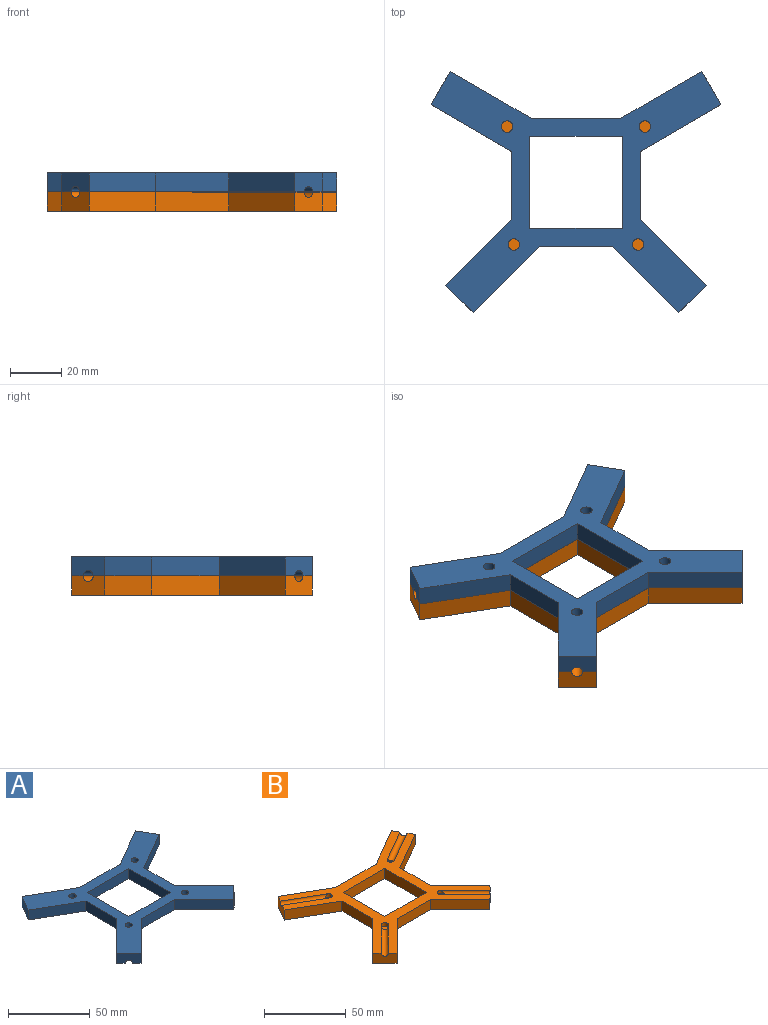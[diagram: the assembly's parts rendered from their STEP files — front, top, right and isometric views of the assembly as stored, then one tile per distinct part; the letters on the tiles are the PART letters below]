
ASSEMBLY  parts=2 mates=1
PART A: 33 faces, bbox 113.2x94.1x7.5 mm
  f0: plane 35x7.5mm, normal (0,1,0), area 260.5mm2, adj f8,f16,f17,f29,f30,f31
  f1: plane 28.79x7.5mm, normal (0,-1,0), area 214.3mm2, adj f2,f16,f23,f29,f31,f32
  f2: plane 25.81x25.81mm, normal (-0.71,-0.71,0), area 273.7mm2, adj f1,f3,f16,f29
  f3: plane 10.61x10.61mm, normal (0.71,-0.71,0), area 104.5mm2, adj f2,f4,f11,f16,f29
  f4: plane 25.81x25.81mm, normal (0.71,0.71,0), area 273.7mm2, adj f3,f5,f16,f29
  f5: plane 26.4x7.5mm, normal (1,0,0), area 198mm2, adj f4,f6,f16,f29
  f6: plane 31.61x18.25mm, normal (0.5,-0.87,0), area 273.7mm2, adj f5,f7,f16,f29
  f7: plane 12.99x7.5mm, normal (0.87,0.5,0), area 104.5mm2, adj f6,f8,f10,f16,f29
  f8: plane 31.61x18.25mm, normal (-0.5,0.87,0), area 273.7mm2, adj f0,f7,f16,f29
  f9: cylinder r=2.25mm len=7.5mm, axis (0,0,1), area 95.9mm2, adj f10,f16,f29
  f10: cylinder r=2.25mm len=28.23mm, axis (0.87,0.5,0), area 201.9mm2, adj f7,f9,f29
  f11: cylinder r=2.25mm len=24.4mm, axis (0.71,-0.71,0), area 201.9mm2, adj f3,f12,f29
  f12: cylinder r=2.25mm len=7.5mm, axis (0,0,1), area 95.9mm2, adj f11,f16,f29
  f13: plane 36x7.5mm, normal (-1,0,0), area 270mm2, adj f14,f15,f16,f29
  f14: plane 36x7.5mm, normal (0,-1,0), area 267.9mm2, adj f13,f16,f28,f29,f30,f31
  f15: plane 36x7.5mm, normal (0,1,0), area 267.9mm2, adj f13,f16,f28,f29,f31,f32
  f16: plane 113.21x94.05mm, normal (0,0,1), area 3120.2mm2, adj f0,f1,f2,f3,f4,f5,f6,f7
  f17: plane 31.61x18.25mm, normal (0.5,0.87,0), area 269.5mm2, adj f0,f16,f18,f31
  f18: plane 12.99x7.5mm, normal (-0.87,0.5,0), area 103.3mm2, adj f16,f17,f19,f24,f31
  f19: plane 31.61x18.25mm, normal (-0.5,-0.87,0), area 269.5mm2, adj f16,f18,f20,f31
  f20: plane 26.4x7.39mm, normal (-1,0,0), area 195mm2, adj f16,f19,f21,f31
  f21: plane 25.81x25.81mm, normal (-0.71,0.71,0), area 269.5mm2, adj f16,f20,f22,f31
  f22: plane 10.61x10.61mm, normal (-0.71,-0.71,0), area 103.3mm2, adj f16,f21,f23,f25,f31
  f23: plane 25.81x25.81mm, normal (0.71,-0.71,0), area 269.5mm2, adj f1,f16,f22,f31
  f24: cylinder r=2.25mm len=28.13mm, axis (-0.87,0.5,0), area 195.1mm2, adj f18,f27,f31
  f25: cylinder r=2.25mm len=24.31mm, axis (-0.71,-0.71,0), area 195.1mm2, adj f22,f26,f31
  f26: cylinder r=2.25mm len=7.39mm, axis (0,0,1), area 95.1mm2, adj f16,f25,f31
  f27: cylinder r=2.25mm len=7.39mm, axis (0,0,1), area 95.1mm2, adj f16,f24,f31
  f28: plane 36x7.39mm, normal (1,0,0), area 265.9mm2, adj f14,f15,f16,f31
  f29: plane 94.05x56.61mm, normal (0,0,-1), area 1306mm2, adj f0,f1,f2,f3,f4,f5,f6,f7
  f30: plane 7x0.11mm, normal (-1,0,0), area 0.8mm2, adj f0,f14,f29,f31
  f31: plane 94.05x56.61mm, normal (0,0,-1), area 1306.3mm2, adj f0,f1,f14,f15,f17,f18,f19,f20
  f32: plane 7x0.11mm, normal (-1,0,0), area 0.8mm2, adj f1,f15,f29,f31
PART B: 34 faces, bbox 113.2x94.1x7.5 mm
  f0: plane 113.21x94.05mm, normal (0,0,-1), area 3183.8mm2, adj f1,f2,f3,f4,f5,f6,f7,f8
  f1: plane 35x7.5mm, normal (0,1,0), area 262.5mm2, adj f0,f2,f16,f33
  f2: plane 31.61x18.25mm, normal (0.5,0.87,0), area 273.7mm2, adj f0,f1,f3,f33
  f3: plane 12.99x7.5mm, normal (-0.87,0.5,0), area 104.5mm2, adj f0,f2,f4,f17,f33
  f4: plane 31.61x18.25mm, normal (-0.5,-0.87,0), area 273.7mm2, adj f0,f3,f5,f33
  f5: plane 26.4x7.5mm, normal (-1,0,0), area 198mm2, adj f0,f4,f6,f33
  f6: plane 25.81x25.81mm, normal (-0.71,0.71,0), area 273.7mm2, adj f0,f5,f7,f33
  f7: plane 10.61x10.61mm, normal (-0.71,-0.71,0), area 104.5mm2, adj f0,f6,f8,f18,f33
  f8: plane 25.81x25.81mm, normal (0.71,-0.71,0), area 273.7mm2, adj f0,f7,f9,f33
  f9: plane 28.79x7.5mm, normal (0,-1,0), area 215.9mm2, adj f0,f8,f10,f33
  f10: plane 25.81x25.81mm, normal (-0.71,-0.71,0), area 273.7mm2, adj f0,f9,f11,f33
  f11: plane 10.61x10.61mm, normal (0.71,-0.71,0), area 104.5mm2, adj f0,f10,f12,f26,f33
  f12: plane 25.81x25.81mm, normal (0.71,0.71,0), area 273.7mm2, adj f0,f11,f13,f33
  f13: plane 26.4x7.5mm, normal (1,0,0), area 198mm2, adj f0,f12,f14,f33
  f14: plane 31.61x18.25mm, normal (0.5,-0.87,0), area 273.7mm2, adj f0,f13,f15,f33
  f15: plane 12.99x7.5mm, normal (0.87,0.5,0), area 104.5mm2, adj f0,f14,f16,f25,f33
  f16: plane 31.61x18.25mm, normal (-0.5,0.87,0), area 273.7mm2, adj f0,f1,f15,f33
  f17: cylinder r=2.25mm len=28.23mm, axis (-0.87,0.5,0), area 201.9mm2, adj f3,f21,f33
  f18: cylinder r=2.25mm len=24.4mm, axis (-0.71,-0.71,0), area 201.9mm2, adj f7,f19,f33
  f19: cylinder r=2.25mm len=4.5mm, axis (0,0,1), area 25.2mm2, adj f18,f20,f33
  f20: plane 4.5x4.5mm, normal (0,0,1), area 15.9mm2, adj f19
  f21: cylinder r=2.25mm len=4.5mm, axis (0,0,1), area 25.2mm2, adj f17,f22,f33
  f22: plane 4.5x4.5mm, normal (0,0,1), area 15.9mm2, adj f21
  f23: plane 4.5x4.5mm, normal (0,0,1), area 15.9mm2, adj f24
  f24: cylinder r=2.25mm len=4.5mm, axis (0,0,1), area 25.2mm2, adj f23,f25,f33
  f25: cylinder r=2.25mm len=28.23mm, axis (0.87,0.5,0), area 201.9mm2, adj f15,f24,f33
  f26: cylinder r=2.25mm len=24.4mm, axis (0.71,-0.71,0), area 201.9mm2, adj f11,f27,f33
  f27: cylinder r=2.25mm len=4.5mm, axis (0,0,1), area 25.2mm2, adj f26,f28,f33
  f28: plane 4.5x4.5mm, normal (0,0,1), area 15.9mm2, adj f27
  f29: plane 36x7.5mm, normal (-1,0,0), area 270mm2, adj f0,f30,f32,f33
  f30: plane 36x7.5mm, normal (0,-1,0), area 270mm2, adj f0,f29,f31,f33
  f31: plane 36x7.5mm, normal (1,0,0), area 270mm2, adj f0,f30,f32,f33
  f32: plane 36x7.5mm, normal (0,1,0), area 270mm2, adj f0,f29,f31,f33
  f33: plane 113.21x94.05mm, normal (0,0,1), area 2612mm2, adj f1,f2,f3,f4,f5,f6,f7,f8
PLACE A t=(0,0,30.8)mm
PLACE B t=(0,0,30.91)mm
MATE planar B.f33 <-> A.f31  axis (0,0,1) through (-18,-18,30.91)mm
